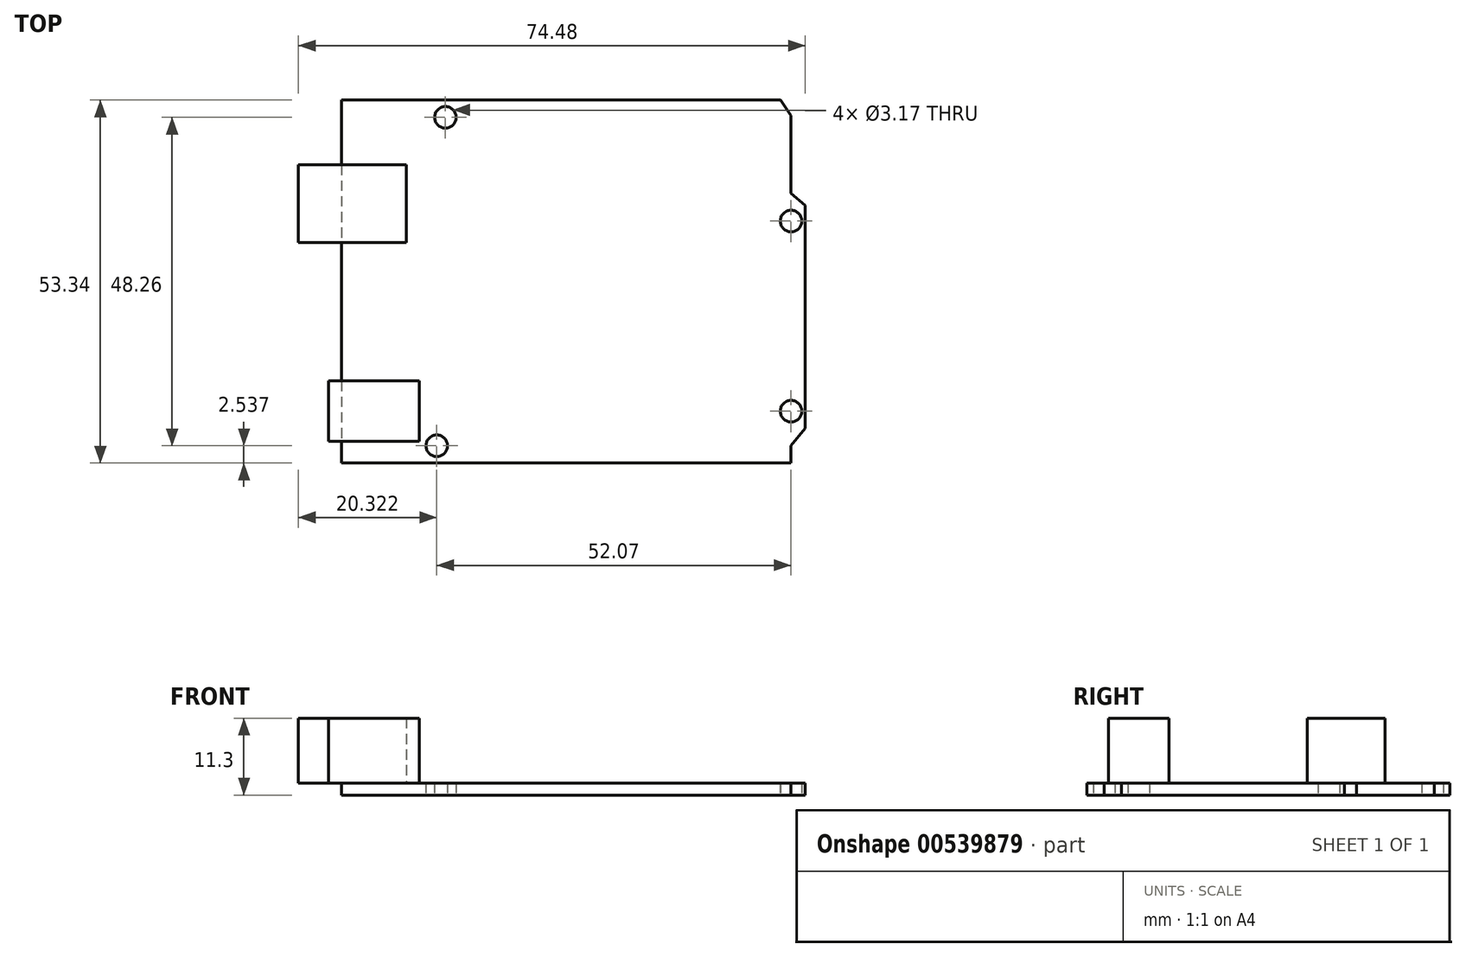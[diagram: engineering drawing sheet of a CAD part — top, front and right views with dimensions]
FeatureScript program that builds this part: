
annotation { "Feature Type Name" : "Feature", "Feature Type Description" : "" }
export const myFeature = defineFeature(function(context is Context, id is Id, definition is map)
    precondition{}
    {
        {
            var Q0;
            Q0=qCreatedBy(makeId("Top.planeOp"),FACE);
            var sketch = newSketch(context, id + "F0", { "sketchPlane" : qUnion([Q0])});
            skLineSegment(sketch, "E0", {"start": v(-32.5, 27) * mm, "end": v(-32.5, -26.34) * mm});
            skLineSegment(sketch, "E1", {"start": v(-32.5, 27) * mm, "end": v(32.02, 27) * mm});
            skLineSegment(sketch, "E2", {"start": v(32.02, 27) * mm, "end": v(33.54, 24.7) * mm});
            skLineSegment(sketch, "E3", {"start": v(-32.5, -26.34) * mm, "end": v(33.54, -26.34) * mm});
            skLineSegment(sketch, "E4", {"start": v(33.54, 24.7) * mm, "end": v(33.54, 13.28) * mm});
            skLineSegment(sketch, "E5", {"start": v(33.54, 13.28) * mm, "end": v(35.63, 11.5) * mm});
            skLineSegment(sketch, "E6", {"start": v(35.63, 11.5) * mm, "end": v(35.63, -21.26) * mm});
            skLineSegment(sketch, "E7", {"start": v(33.54, -26.34) * mm, "end": v(33.54, -23.8) * mm});
            skLineSegment(sketch, "E8", {"start": v(33.54, -23.8) * mm, "end": v(35.63, -21.26) * mm});
            skCircle(sketch, "E9", {"center": v(33.54, -18.72) * mm, "radius": 1.59 * mm});
            skLineSegment(sketch, "E10", {"start": v(33.54, -18.72) * mm, "end": v(33.54, -17.14) * mm});
            skCircle(sketch, "E11", {"center": v(33.54, 9.22) * mm, "radius": 1.59 * mm});
            skCircle(sketch, "E12", {"center": v(-18.53, -23.8) * mm, "radius": 1.59 * mm});
            skPoint(sketch, "E13.start.orphan", {"position": v(-18.53, -26.34) * mm});
            skLineSegment(sketch, "E14", {"start": v(-17.26, -26.34) * mm, "end": v(-17.26, -22.85) * mm});
            skCircle(sketch, "E15", {"center": v(-17.26, 24.46) * mm, "radius": 1.59 * mm});
            skSolve(sketch);
        }
        {
            var Q0;
            Q0 = qSketchRegion(id + "F0", true);
            extrude(context, id + "F1", {"entities" : qUnion([Q0]), "depth" : 1.78 * mm, "offsetDistance" : 25.4 * mm});
        }
        {
            var Q0;
            Q0=makeQuery(id+"F1.opExtrude","CAP_FACE",FACE,{"disambiguationData":[OSD([sQuery(id+"F0.wireOp",EDGE,"E0"),sQuery(id+"F0.wireOp",EDGE,"E1"),sQuery(id+"F0.wireOp",EDGE,"E2"),sQuery(id+"F0.wireOp",EDGE,"E3"),sQuery(id+"F0.wireOp",EDGE,"E4"),sQuery(id+"F0.wireOp",EDGE,"E5"),sQuery(id+"F0.wireOp",EDGE,"E6"),sQuery(id+"F0.wireOp",EDGE,"E8"),sQuery(id+"F0.wireOp",EDGE,"E7"),sQuery(id+"F0.wireOp",EDGE,"E9"),sQuery(id+"F0.wireOp",EDGE,"E11"),sQuery(id+"F0.wireOp",EDGE,"E12"),sQuery(id+"F0.wireOp",EDGE,"E15")])],"isStart":false});
            var sketch = newSketch(context, id + "F2", { "sketchPlane" : qUnion([Q0])});
            skPoint(sketch, "E16.orphan", {"position": v(-39.38, -26.36) * mm});
            skPoint(sketch, "E17.end.orphan", {"position": v(-45.76, -26.36) * mm});
            skPoint(sketch, "E18.start.orphan", {"position": v(-33, -26.36) * mm});
            skLineSegment(sketch, "E19", {"start": v(-23.15, 6.04) * mm, "end": v(-23.15, 6.04) * mm});
            skPoint(sketch, "E20.start.orphan", {"position": v(-32.68, 6.04) * mm});
            skLineSegment(sketch, "E21", {"start": v(-32.5, 6.04) * mm, "end": v(-22.97, 6.04) * mm});
            skLineSegment(sketch, "E22", {"start": v(-22.97, 6.04) * mm, "end": v(-22.97, 17.47) * mm});
            skPoint(sketch, "E23.end.orphan", {"position": v(-35, 6.04) * mm});
            skLineSegment(sketch, "E24", {"start": v(-22.97, 17.47) * mm, "end": v(-38.85, 17.47) * mm});
            skLineSegment(sketch, "E25", {"start": v(-38.85, 17.47) * mm, "end": v(-38.85, 6.04) * mm});
            skLineSegment(sketch, "E26", {"start": v(-32.5, 6.04) * mm, "end": v(-38.85, 6.04) * mm});
            skPoint(sketch, "E27.end.orphan", {"position": v(-21.57, -17.47) * mm});
            skPoint(sketch, "E28.start.orphan", {"position": v(-21.57, -23.17) * mm});
            skLineSegment(sketch, "E29", {"start": v(-32.5, -23.17) * mm, "end": v(-21.07, -23.17) * mm});
            skPoint(sketch, "E30.end.orphan", {"position": v(-34.9, -17.47) * mm});
            skPoint(sketch, "E31.end.orphan", {"position": v(-34.9, -26.36) * mm});
            skPoint(sketch, "E32.end.orphan", {"position": v(-21.57, -26.35) * mm});
            skLineSegment(sketch, "E33", {"start": v(-34.4, -23.17) * mm, "end": v(-32.5, -23.17) * mm});
            skLineSegment(sketch, "E34", {"start": v(-34.4, -23.17) * mm, "end": v(-34.4, -14.28) * mm});
            skLineSegment(sketch, "E35", {"start": v(-34.4, -14.28) * mm, "end": v(-21.07, -14.28) * mm});
            skLineSegment(sketch, "E36", {"start": v(-21.07, -14.28) * mm, "end": v(-21.07, -23.17) * mm});
            skPoint(sketch, "E37.end.orphan", {"position": v(-14.78, 6.04) * mm});
            skPoint(sketch, "E37.start.orphan", {"position": v(-14.78, -26.36) * mm});
            skPoint(sketch, "E38.end.orphan", {"position": v(-19.07, -23.17) * mm});
            skPoint(sketch, "E38.start.orphan", {"position": v(-19.07, -26.35) * mm});
            skLineSegment(sketch, "E39", {"start": v(-32.5, 27) * mm, "end": v(-32.5, 17.47) * mm});
            skSolve(sketch);
        }
        {
            var Q0;
            Q0 = qSketchRegion(id + "F2", true);
            extrude(context, id + "F3", {"entities" : qUnion([Q0]), "depth" : 9.52 * mm, "offsetDistance" : 25.4 * mm});
        }
    });
